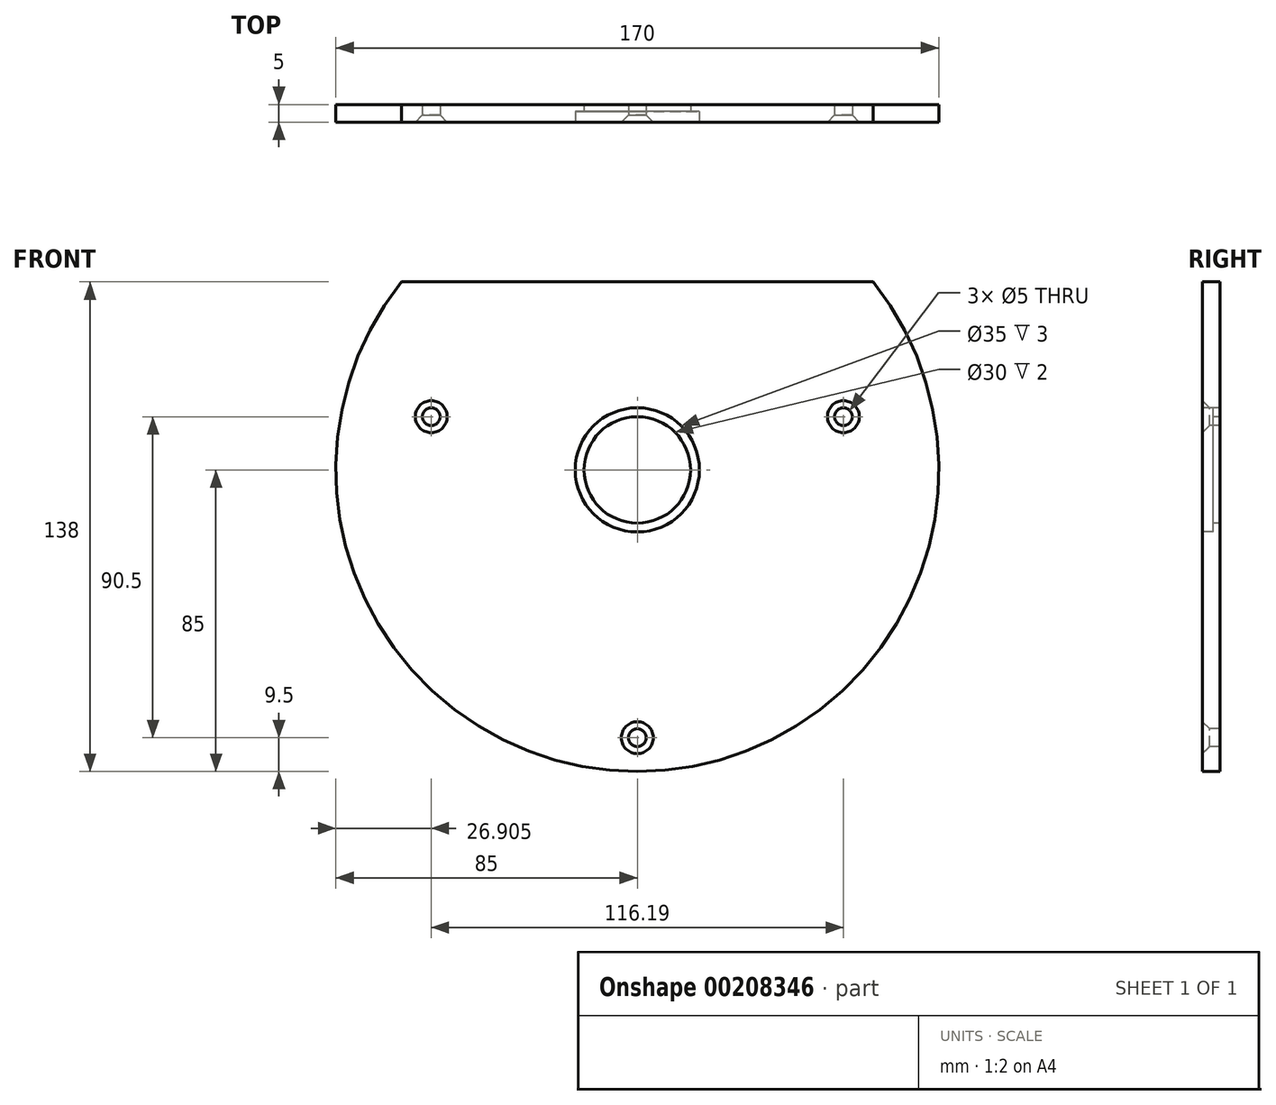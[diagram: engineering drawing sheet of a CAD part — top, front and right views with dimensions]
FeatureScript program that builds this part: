
annotation { "Feature Type Name" : "Feature", "Feature Type Description" : "" }
export const myFeature = defineFeature(function(context is Context, id is Id, definition is map)
    precondition{}
    {
        {
            assignVariable(context, id + "F0", {"name" : "dia", "anyValue" : 5});
        }
        {
            var Q0;
            Q0=qCreatedBy(makeId("Front.planeOp"),FACE);
            var sketch = newSketch(context, id + "F1", { "sketchPlane" : qUnion([Q0])});
            skArc(sketch, "E0", {"start": v(-66.45, 53) * mm, "mid": v(0, -85) * mm, "end": v(66.45, 53) * mm});
            skCircle(sketch, "E1", {"center": v(0, 0) * mm, "radius": 15 * mm});
            skCircle(sketch, "E2", {"center": v(0, 0) * mm, "radius": 17.5 * mm});
            skLineSegment(sketch, "E3", {"start": v(-66.45, 53) * mm, "end": v(66.45, 53) * mm});
            skCircle(sketch, "E4", {"center": v(0, 0) * mm, "radius": 60 * mm, "construction": true});
            skCircle(sketch, "E5", {"center": v(0, 0) * mm, "radius": 75.5 * mm, "construction": true});
            skLineSegment(sketch, "E6", {"start": v(-58.1, 15) * mm, "end": v(58.1, 15) * mm, "construction": true});
            skCircle(sketch, "E7", {"center": v(-58.1, 15) * mm, "radius": 2.5 * mm});
            skCircle(sketch, "E8", {"center": v(58.1, 15) * mm, "radius": 2.5 * mm});
            skCircle(sketch, "E9", {"center": v(0, -75.5) * mm, "radius": 2.5 * mm});
            skLineSegment(sketch, "E10", {"start": v(-58.1, 15) * mm, "end": v(0, 0) * mm, "construction": true});
            skLineSegment(sketch, "E11", {"start": v(58.1, 15) * mm, "end": v(0, 0) * mm, "construction": true});
            skSolve(sketch);
        }
        {
            var Q0;
            Q0 = qSketchRegion(id + "F1", true);
            var Q1;
            Q1=makeQuery(id+"F1.imprint","IMPRINT",FACE,{"disambiguationData":[TD([[makeQuery(id+"F1.imprint","IMPRINT",EDGE,{"derivedFrom":sQuery(id+"F1.wireOp",EDGE,"E7")}),1.0]])]});
            var Q2;
            Q2=makeQuery(id+"F1.imprint","IMPRINT",FACE,{"disambiguationData":[TD([[makeQuery(id+"F1.imprint","IMPRINT",EDGE,{"derivedFrom":sQuery(id+"F1.wireOp",EDGE,"E8")}),1.0]])]});
            var Q3;
            Q3=makeQuery(id+"F1.imprint","IMPRINT",FACE,{"disambiguationData":[TD([[makeQuery(id+"F1.imprint","IMPRINT",EDGE,{"derivedFrom":sQuery(id+"F1.wireOp",EDGE,"E9")}),1.0]])]});
            extrude(context, id + "F2", {"entities" : qUnion([Q0, Q1, Q2, Q3]), "oppositeDirection" : true, "depth" : 5 * mm});
        }
        {
            var Q0;
            Q0=makeQuery(id+"F1.imprint","IMPRINT",FACE,{"disambiguationData":[TD([[makeQuery(id+"F1.imprint","IMPRINT",EDGE,{"derivedFrom":sQuery(id+"F1.wireOp",EDGE,"E1")}),-1.0]])]});
            extrude(context, id + "F3", {"entities" : qUnion([Q0]), "operationType" : NewBodyOperationType.ADD, "oppositeDirection" : true, "depth" : 5 * mm, "hasSecondDirection" : true, "secondDirectionOppositeDirection" : true, "secondDirectionDepth" : 3 * mm});
        }
        {
            var Q0;
            Q0=sQuery(id+"F1.wireOp",VERTEX,"E7.center");
            var Q1;
            Q1=sQuery(id+"F1.wireOp",VERTEX,"E11.start");
            var Q2;
            Q2=sQuery(id+"F1.wireOp",VERTEX,"E9.center");
            var Q3;
            Q3=makeQuery(id+"F2.opExtrude","SWEPT_BODY",BODY,{"disambiguationData":[OSD([sQuery(id+"F1.wireOp",EDGE,"E0"),sQuery(id+"F1.wireOp",EDGE,"E2"),sQuery(id+"F1.wireOp",EDGE,"E3")])]});
            hole(context, id + "F4", {"style" : HoleStyle.C_SINK, "endStyle" : HoleEndStyle.THROUGH, "holeDiameter" : getVariable(context, 'dia') * mm, "cSinkDiameter" : 9 * mm, "cSinkAngle" : 90 * degree, "locations" : qUnion([Q0, Q1, Q2]), "scope" : qUnion([Q3]), "isTappedThrough" : true});
        }
    });
